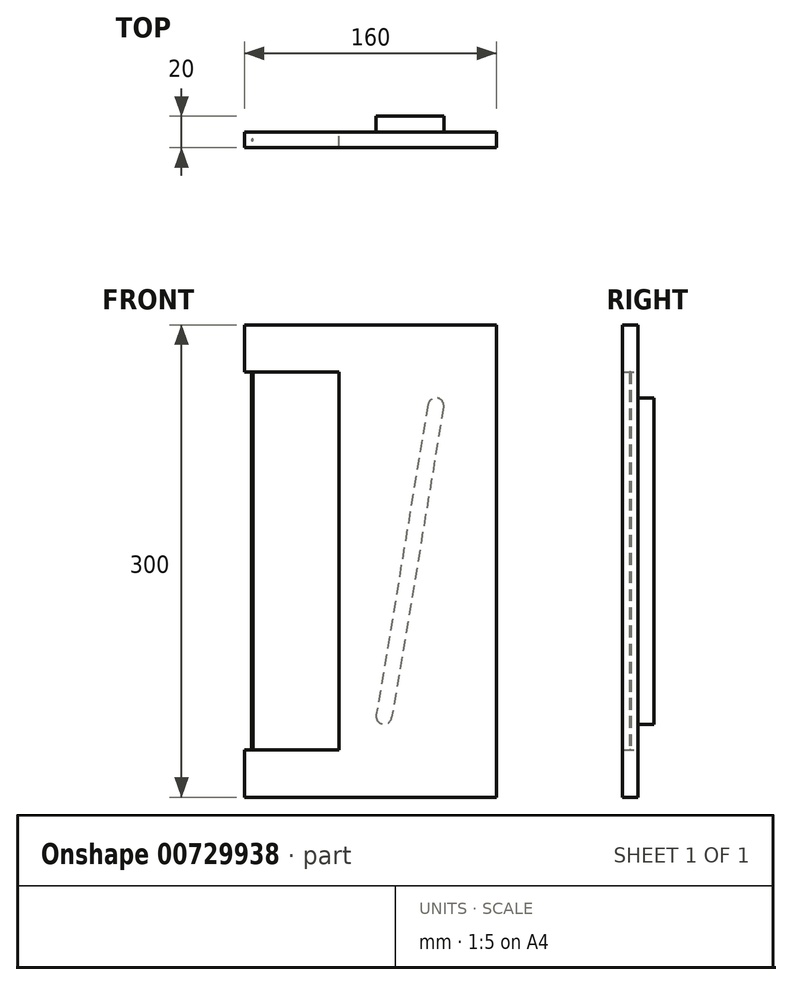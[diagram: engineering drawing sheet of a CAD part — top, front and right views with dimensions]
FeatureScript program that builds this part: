
annotation { "Feature Type Name" : "Feature", "Feature Type Description" : "" }
export const myFeature = defineFeature(function(context is Context, id is Id, definition is map)
    precondition{}
    {
        {
            var Q0;
            Q0=qCreatedBy(makeId("Front.planeOp"),FACE);
            var sketch = newSketch(context, id + "F0", { "sketchPlane" : qUnion([Q0])});
            skLineSegment(sketch, "E0", {"start": v(142.25, 125.92) * mm, "end": v(142.25, -114.08) * mm});
            skLineSegment(sketch, "E1", {"start": v(142.25, -144.08) * mm, "end": v(242.25, -144.08) * mm});
            skLineSegment(sketch, "E2", {"start": v(242.25, -144.08) * mm, "end": v(242.25, 155.92) * mm});
            skLineSegment(sketch, "E3", {"start": v(242.25, 155.92) * mm, "end": v(142.25, 155.92) * mm});
            skLineSegment(sketch, "E4", {"start": v(142.25, 155.92) * mm, "end": v(82.25, 155.92) * mm});
            skLineSegment(sketch, "E5", {"start": v(82.25, 155.92) * mm, "end": v(82.25, 125.92) * mm});
            skLineSegment(sketch, "E6", {"start": v(82.25, 125.92) * mm, "end": v(142.25, 125.92) * mm});
            skLineSegment(sketch, "E7", {"start": v(142.25, -144.08) * mm, "end": v(82.25, -144.08) * mm});
            skLineSegment(sketch, "E8", {"start": v(82.25, -144.08) * mm, "end": v(82.25, -114.08) * mm});
            skLineSegment(sketch, "E9", {"start": v(82.25, -114.08) * mm, "end": v(142.25, -114.08) * mm});
            skPoint(sketch, "E10.orphan", {"position": v(192.25, 155.92) * mm});
            skPoint(sketch, "E11.orphan", {"position": v(192.25, -144.08) * mm});
            skSolve(sketch);
        }
        {
            var Q0;
            Q0=makeQuery(id+"F0.imprint","IMPRINT",FACE,{"disambiguationData":[TD([[makeQuery(id+"F0.imprint","IMPRINT",EDGE,{"derivedFrom":sQuery(id+"F0.wireOp",EDGE,"E0")}),1.0]])]});
            extrude(context, id + "F1", {"entities" : qUnion([Q0]), "depth" : 10 * mm, "offsetDistance" : 25 * mm});
        }
        {
            var Q0;
            Q0=makeQuery(id+"F1.opExtrude","SWEPT_FACE",FACE,{"disambiguationData":[OSD([sQuery(id+"F0.wireOp",EDGE,"E9")])]});
            var sketch = newSketch(context, id + "F2", { "sketchPlane" : qUnion([Q0])});
            skCircle(sketch, "E12", {"center": v(87.25, -5) * mm, "radius": 0.5 * mm});
            skPoint(sketch, "E12.centerSnap0", {"position": v(82.25, -5) * mm});
            skSolve(sketch);
        }
        {
            var Q0;
            Q0 = qSketchRegion(id + "F2", true);
            extrude(context, id + "F3", {"entities" : qUnion([Q0]), "operationType" : NewBodyOperationType.ADD, "endBound" : BoundingType.UP_TO_NEXT, "depth" : 25 * mm, "offsetDistance" : 25 * mm});
        }
        {
            var Q0;
            Q0=makeQuery(id+"F1.opExtrude","CAP_FACE",FACE,{"disambiguationData":[OSD([sQuery(id+"F0.wireOp",EDGE,"E0"),sQuery(id+"F0.wireOp",EDGE,"E1"),sQuery(id+"F0.wireOp",EDGE,"E2"),sQuery(id+"F0.wireOp",EDGE,"E3"),sQuery(id+"F0.wireOp",EDGE,"E4"),sQuery(id+"F0.wireOp",EDGE,"E5"),sQuery(id+"F0.wireOp",EDGE,"E6"),sQuery(id+"F0.wireOp",EDGE,"E7"),sQuery(id+"F0.wireOp",EDGE,"E8"),sQuery(id+"F0.wireOp",EDGE,"E9")])],"isStart":false});
            var sketch = newSketch(context, id + "F4", { "sketchPlane" : qUnion([Q0])});
            skLineSegment(sketch, "E13", {"start": v(187.3, 155.92) * mm, "end": v(187.3, -144.08) * mm, "construction": true});
            skPoint(sketch, "E14", {"position": v(187.3, 5.92) * mm});
            skLineSegment(sketch, "E15", {"start": v(203.81, 104.55) * mm, "end": v(170.8, -92.7) * mm, "construction": true});
            skArc(sketch, "E16.0.startCap", {"start": v(198.88, 105.37) * mm, "mid": v(204.64, 109.48) * mm, "end": v(208.74, 103.72) * mm});
            skArc(sketch, "E16.0.endCap", {"start": v(175.73, -93.53) * mm, "mid": v(169.98, -97.64) * mm, "end": v(165.87, -91.88) * mm});
            skLineSegment(sketch, "E16.0.left", {"start": v(208.74, 103.72) * mm, "end": v(175.73, -93.53) * mm});
            skLineSegment(sketch, "E16.0.right", {"start": v(198.88, 105.37) * mm, "end": v(165.87, -91.88) * mm});
            skSolve(sketch);
        }
        {
            var Q0;
            Q0 = qSketchRegion(id + "F4", true);
            extrude(context, id + "F5", {"entities" : qUnion([Q0]), "operationType" : NewBodyOperationType.ADD, "oppositeDirection" : true, "depth" : 20 * mm, "offsetDistance" : 25 * mm});
        }
    });
